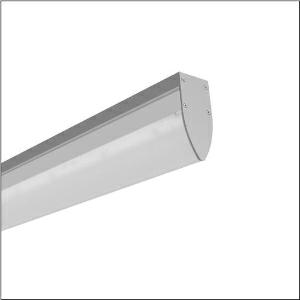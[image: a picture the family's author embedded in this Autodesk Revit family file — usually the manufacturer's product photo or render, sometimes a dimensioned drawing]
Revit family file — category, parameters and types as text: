
# Revit family: mira_r__21_td_51fr527d424a_f4a9
name_source: partatom
category: Lighting Fixtures
units: mm (PartAtom-declared; Revit-internal decimal feet)

## family parameters
Cut with Voids When Loaded = No
Host = Face
Light Source = No
Part Type = Normal
Room Calculation Point = No
Round Connector Dimension = Use Diameter
Shared = No

## types (1)
- Mira® 21 TD (1 x LED, 2020 lm, 14 W, 4000K)
    Apparent Load = 14 VA
    CIE Flux Codes = 40 68 87 81 100
    Color Rendering = 80
    Color Temperature = 4000K
    Default Elevation = 1800 mm
    Description = Mira® 21 TD, clean room luminaire, primary light control with reflector, primary optical cover: cover, of PMMA, frosted, light emission: direct distribution, primary light characteristic: symmetric, installation type: surface-mounted, LED, rated luminous flux: 2.020lm, luminous efficacy: 144lm/W, light colour: 840, colour temperature: 4000K, control gear: ECG, with terminal, 3-pole, max. 2.5mm², mains connection: 230V, AC, 50/60Hz, rated input power: 14W, luminaire housing, of sheet steel, coated, pure white (RAL 9010), length: 600mm, width: 55mm, height: 120mm, protection rating (complete): IP43, insulation class (complete): insulation class I (protective earthing), certification: CE, UKCA, permissible operating ambient temperature: -5..+40°C, standard: EN 50419, packaging unit: 1 piece
    Height = 0 mm  [stored 0 ft]
    Lamp = 1 x LED
    Lamp Light Flux = 2020 lm
    Lamp Power = 14 W
    Lamp count = 1
    Length = 600 mm
    Luminous efficacy = 144 lm/W
    Manufacturer = Siteco
    ModVariant = No
    Model = 51FR527D424A
    Mounting Place = Ceiling
    Mounting Type = Recessed
    Number of Poles = 1
    OnlyDefault = Yes
    Power Factor = 1
    Product Name = Mira® 21 TD
    Product group = clean room luminaire
    ProductGroupID = 402
    Protection Class = Protection class I
    Protection Degree = IP 43
    RLX_Detail_Level = 1
    RLX_Emergency_Light_Flux = 0 lm
    RLX_Emergency_Type = 0
    RLX_Emergency_Type_DB = No
    RlxData = <blob elided: 25833 chars, md5=12749cdd>
    Socket = socket
    Standby Power = 0 W
    System Light Flux = 2020 lm
    System Power = 14 W
    Type Comments = Product without accessories
    Type Image = l_1007115.jpg
    URL = http://relux.com
    VarID = ---
    Voltage = 0 V
    Weight = 0.00 kg
    Width = 55 mm

note: [stored X ft] marks values corroborated as IEEE doubles in the binary element streams (Revit-internal decimal feet)

## geometry (parser evidence)
native form markers: Blend x4, Sweep x12
no freeform markers — native parametric forms only
